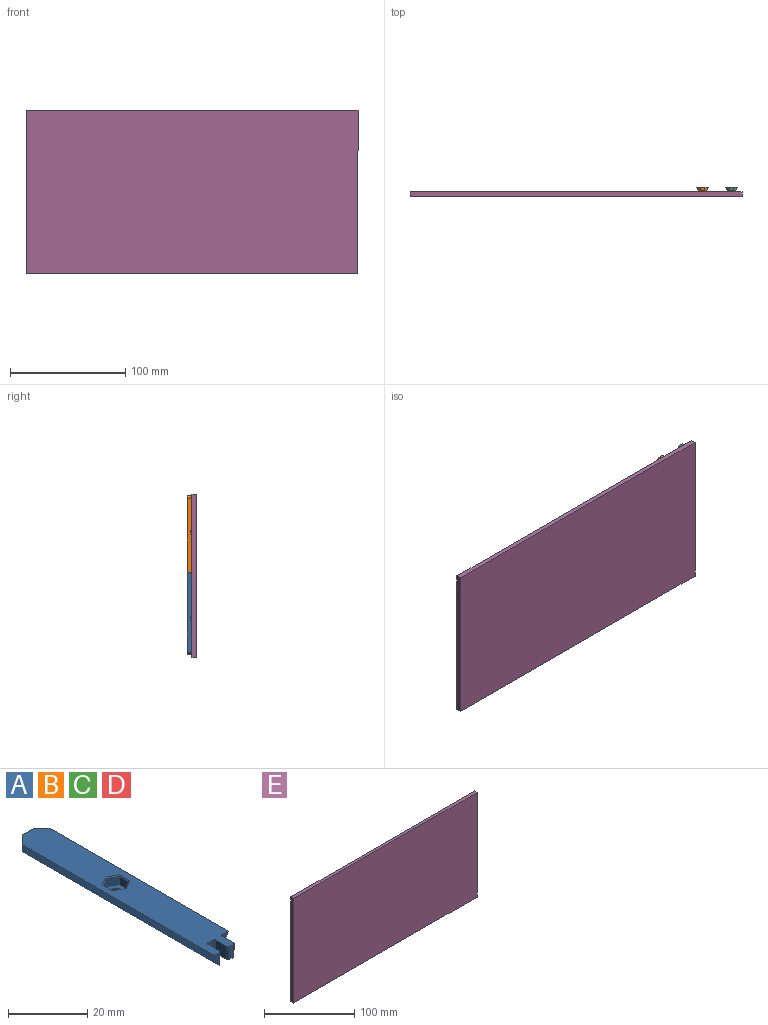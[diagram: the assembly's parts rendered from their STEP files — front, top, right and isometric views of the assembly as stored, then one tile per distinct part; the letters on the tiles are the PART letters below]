
ASSEMBLY  parts=5 mates=4
PART A: 35 faces, bbox 10x71.4x4 mm
  f0: plane 71.4x10mm, normal (0,0,1), area 644.8mm2, adj f1,f2,f11,f12,f13,f14,f15,f16
  f1: plane 4x3mm, normal (0,1,0), area 12mm2, adj f0,f32,f33,f34
  f2: plane 65.27x4mm, normal (0.91,0,-0.42), area 283.9mm2, adj f0,f3,f24,f32
  f3: plane 70.4x6.27mm, normal (0,0,-1), area 416.1mm2, adj f2,f17,f18,f19,f20,f21,f22,f23
  f4: plane 2.82x2.47mm, normal (-0.5,-0.87,0), area 8mm2, adj f5,f9,f10,f11
  f5: plane 2.82x2.47mm, normal (0.5,-0.87,0), area 8mm2, adj f4,f6,f10,f12
  f6: plane 3.26x2.47mm, normal (1,0,0), area 8mm2, adj f5,f7,f10,f13
  f7: plane 2.82x2.47mm, normal (0.5,0.87,0), area 8mm2, adj f6,f8,f10,f14
  f8: plane 2.82x2.47mm, normal (-0.5,0.87,0), area 8mm2, adj f7,f9,f10,f15
  f9: plane 3.26x2.47mm, normal (-1,0,0), area 8mm2, adj f4,f8,f10,f16
  f10: plane 6.51x5.64mm, normal (0,0,1), area 19.5mm2, adj f4,f5,f6,f7,f8,f9,f17
  f11: plane 3.12x1.97mm, normal (-0.35,-0.61,0.71), area 1.5mm2, adj f0,f4,f12,f16
  f12: plane 3.12x1.97mm, normal (0.35,-0.61,0.71), area 1.5mm2, adj f0,f5,f11,f13
  f13: plane 3.6x0.3mm, normal (0.71,0,0.71), area 1.5mm2, adj f0,f6,f12,f14
  f14: plane 3.12x1.97mm, normal (0.35,0.61,0.71), area 1.5mm2, adj f0,f7,f13,f15
  f15: plane 3.12x1.97mm, normal (-0.35,0.61,0.71), area 1.5mm2, adj f0,f8,f14,f16
  f16: plane 3.6x0.3mm, normal (-0.71,0,0.71), area 1.5mm2, adj f0,f9,f11,f15
  f17: cylinder r=1.6mm len=3.2mm, axis (0,0,1), area 12.4mm2, adj f3,f10
  f18: plane 70.27x4mm, normal (-0.91,0,-0.42), area 306mm2, adj f0,f3,f19,f33
  f19: plane 4x1.9mm, normal (0,-1,0), area 3.9mm2, adj f0,f3,f18,f26
  f20: plane 4x4mm, normal (1,0,0), area 16mm2, adj f0,f3,f26,f27
  f21: plane 4x1.7mm, normal (0,-1,0), area 6.8mm2, adj f0,f3,f27,f28
  f22: plane 4x4mm, normal (-1,0,0), area 16mm2, adj f0,f3,f28,f29
  f23: plane 4x1.3mm, normal (0,-1,0), area 5.2mm2, adj f0,f3,f29,f30
  f24: plane 4x2.1mm, normal (0,-1,0), area 4.7mm2, adj f0,f2,f3,f31
  f25: plane 4x4mm, normal (1,0,0), area 16mm2, adj f0,f3,f30,f31
  f26: cylinder r=0.5mm len=4mm, axis (0,0,1), area 3.1mm2, adj f0,f3,f19,f20
  f27: cylinder r=0.5mm len=4mm, axis (0,0,1), area 3.1mm2, adj f0,f3,f20,f21
  f28: cylinder r=0.5mm len=4mm, axis (0,0,1), area 3.1mm2, adj f0,f3,f21,f22
  f29: cylinder r=0.5mm len=4mm, axis (0,0,1), area 3.1mm2, adj f0,f3,f22,f23
  f30: cylinder r=0.5mm len=4mm, axis (0,0,1), area 3.1mm2, adj f0,f3,f23,f25
  f31: cylinder r=0.5mm len=4mm, axis (0,0,1), area 3.1mm2, adj f0,f3,f24,f25
  f32: plane 4x3mm, normal (0.71,0.71,0), area 11mm2, adj f0,f1,f2,f3,f34
  f33: plane 4x3mm, normal (-0.71,0.71,0), area 11mm2, adj f0,f1,f3,f18,f34
  f34: plane 6x1mm, normal (0,0.71,-0.71), area 7.1mm2, adj f1,f3,f32,f33
PART B: same geometry as A
PART C: same geometry as A
PART D: same geometry as A
PART E: 6 faces, bbox 288.4x4.1x142.2 mm
  f0: plane 288.4x4.1mm, normal (0,0,-1), area 1182.4mm2, adj f1,f2,f3,f4
  f1: plane 288.4x142.2mm, normal (0,-1,0), area 41010.5mm2, adj f0,f2,f4,f5
  f2: plane 142.2x4.1mm, normal (1,0,0), area 583mm2, adj f0,f1,f3,f5
  f3: plane 288.4x142.2mm, normal (0,1,0), area 41010.5mm2, adj f0,f2,f4,f5
  f4: plane 142.2x4.1mm, normal (-1,0,0), area 583mm2, adj f0,f1,f3,f5
  f5: plane 288.4x4.1mm, normal (0,0,1), area 1182.4mm2, adj f1,f2,f3,f4
PLACE A rot(axis=(-1,0,0),90deg) t=(-48.92,-206.89,164.14)mm
PLACE B rot(axis=(0,-0.71,-0.71),180deg) t=(-48.92,-206.89,313.94)mm
PLACE C rot(axis=(0,0.71,0.71),180deg) t=(-23.92,-206.89,313.94)mm
PLACE D rot(axis=(-1,0,0),90deg) t=(-23.92,-206.89,164.14)mm
PLACE E t=(-307.12,-210.99,309.54)mm
MATE fastened E.f3 <-> D.f3  axis (0,1,0) through (-158.92,-206.89,167.34)mm
MATE fastened B.f23 <-> A.f21  axis (0,0,-1) through (-50.17,-204.89,236.54)mm
MATE fastened E.f3 <-> A.f3  axis (0,1,0) through (-158.92,-206.89,167.34)mm
MATE fastened D.f21 <-> C.f23  axis (0,0,1) through (-25.17,-204.89,236.54)mm
